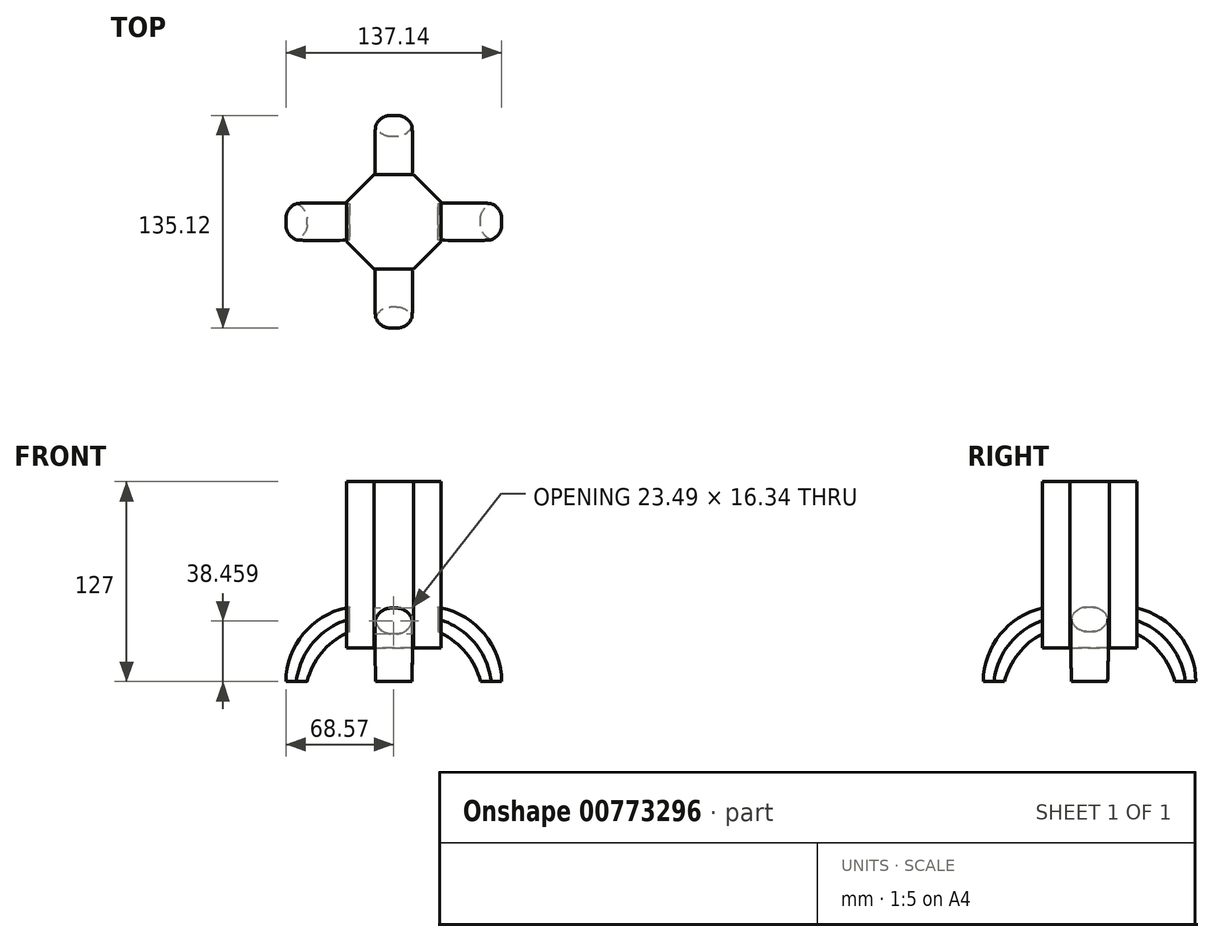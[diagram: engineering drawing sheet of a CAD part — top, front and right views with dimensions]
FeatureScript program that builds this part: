
annotation { "Feature Type Name" : "Feature", "Feature Type Description" : "" }
export const myFeature = defineFeature(function(context is Context, id is Id, definition is map)
    precondition{}
    {
        {
            var Q0;
            Q0=qCreatedBy(makeId("Top.planeOp"),FACE);
            var sketch = newSketch(context, id + "F0", { "sketchPlane" : qUnion([Q0])});
            skCircle(sketch, "E0.cCircle", {"center": v(0, 0) * mm, "radius": 30.08 * mm, "construction": true});
            skLineSegment(sketch, "E0.0", {"start": v(30.08, 12.46) * mm, "end": v(30.08, -12.46) * mm});
            skLineSegment(sketch, "E0.1", {"start": v(30.08, -12.46) * mm, "end": v(12.46, -30.08) * mm});
            skLineSegment(sketch, "E0.2", {"start": v(12.46, -30.08) * mm, "end": v(-12.46, -30.08) * mm});
            skLineSegment(sketch, "E0.3", {"start": v(-12.46, -30.08) * mm, "end": v(-30.08, -12.46) * mm});
            skLineSegment(sketch, "E0.4", {"start": v(-30.08, -12.46) * mm, "end": v(-30.08, 12.46) * mm});
            skLineSegment(sketch, "E0.5", {"start": v(-30.08, 12.46) * mm, "end": v(-12.46, 30.08) * mm});
            skLineSegment(sketch, "E0.6", {"start": v(-12.46, 30.08) * mm, "end": v(12.46, 30.08) * mm});
            skLineSegment(sketch, "E0.7", {"start": v(12.46, 30.08) * mm, "end": v(30.08, 12.46) * mm});
            skPoint(sketch, "E0.0.midPoint", {"position": v(30.08, 0) * mm});
            skSolve(sketch);
        }
        {
            var Q0;
            Q0 = qSketchRegion(id + "F0", true);
            extrude(context, id + "F1", {"entities" : qUnion([Q0]), "depth" : 127 * mm, "offsetDistance" : 25.4 * mm, "hasSecondDirection" : true, "secondDirectionOppositeDirection" : false, "secondDirectionDepth" : 21.34 * mm});
        }
        {
            var Q0;
            Q0=qCreatedBy(makeId("Front.planeOp"),FACE);
            var sketch = newSketch(context, id + "F2", { "sketchPlane" : qUnion([Q0])});
            skLineSegment(sketch, "E1", {"start": v(0, 0) * mm, "end": v(0, 165.92) * mm, "construction": true});
            skLineSegment(sketch, "E2", {"start": v(0, 165.92) * mm, "end": v(30.07, 127) * mm});
            skLineSegment(sketch, "E3", {"start": v(30.07, 127) * mm, "end": v(0, 127) * mm});
            skSolve(sketch);
        }
        {
            var Q0;
            Q0 = qSketchRegion(id + "F2", true);
            var Q1;
            Q1=sQuery(id+"F2.wireOp",EDGE,"E2");
            var Q2;
            Q2=sQuery(id+"F2.wireOp",EDGE,"E3");
            var Q3;
            Q3=sQuery(id+"F2.wireOp",EDGE,"E1");
            revolve(context, id + "F3", {"bodyType" : ToolBodyType.SURFACE, "surfaceOperationType" : NewSurfaceOperationType.NEW, "entities" : qUnion([Q0]), "surfaceEntities" : qUnion([Q1, Q2]), "axis" : qUnion([Q3]), "revolveType" : RevolveType.FULL});
        }
        {
            var Q0;
            Q0=qCreatedBy(makeId("Front.planeOp"),FACE);
            var sketch = newSketch(context, id + "F4", { "sketchPlane" : qUnion([Q0])});
            skArc(sketch, "E4", {"start": v(-28.1, 47.23) * mm, "mid": v(-56.89, 30.94) * mm, "end": v(-68.57, 0) * mm});
            skArc(sketch, "E5", {"start": v(-28.01, 31.76) * mm, "mid": v(-45.21, 19) * mm, "end": v(-55.09, 0) * mm});
            skLineSegment(sketch, "E6", {"start": v(-68.57, 0) * mm, "end": v(-55.09, 0) * mm});
            skLineSegment(sketch, "E7", {"start": v(-28.1, 47.23) * mm, "end": v(-28.01, 31.76) * mm});
            skLineSegment(sketch, "E8.MirrorCS", {"start": v(68.57, 0) * mm, "end": v(55.09, 0) * mm});
            skArc(sketch, "E9.MirrorCS", {"start": v(28.1, 47.23) * mm, "mid": v(56.89, 30.94) * mm, "end": v(68.57, 0) * mm});
            skLineSegment(sketch, "E10.MirrorCS", {"start": v(28.1, 47.23) * mm, "end": v(28.01, 31.76) * mm});
            skArc(sketch, "E11.MirrorCS", {"start": v(28.01, 31.76) * mm, "mid": v(45.21, 19) * mm, "end": v(55.09, 0) * mm});
            skSolve(sketch);
        }
        {
            var Q0;
            Q0=makeQuery(id+"F4.imprint","IMPRINT",FACE,{"disambiguationData":[TD([[makeQuery(id+"F4.imprint","IMPRINT",EDGE,{"derivedFrom":sQuery(id+"F4.wireOp",EDGE,"E4")}),1.0]])]});
            var Q1;
            Q1=makeQuery(id+"F4.imprint","IMPRINT",FACE,{"disambiguationData":[TD([[makeQuery(id+"F4.imprint","IMPRINT",EDGE,{"derivedFrom":sQuery(id+"F4.wireOp",EDGE,"E8.MirrorCS")}),-1.0]])]});
            extrude(context, id + "F5", {"entities" : qUnion([Q0, Q1]), "endBound" : BoundingType.SYMMETRIC, "depth" : 24.13 * mm, "offsetDistance" : 25.4 * mm});
        }
        {
            var Q0;
            Q0=makeQuery(id+"F5.opExtrude","CAP_EDGE",EDGE,{"disambiguationData":[OSD([sQuery(id+"F4.wireOp",EDGE,"E4")])],"isStart":false});
            var Q1;
            Q1=makeQuery(id+"F5.opExtrude","CAP_EDGE",EDGE,{"disambiguationData":[OSD([sQuery(id+"F4.wireOp",EDGE,"E5")])],"isStart":false});
            var Q2;
            Q2=makeQuery(id+"F5.opExtrude","CAP_EDGE",EDGE,{"disambiguationData":[OSD([sQuery(id+"F4.wireOp",EDGE,"E4")])],"isStart":true});
            var Q3;
            Q3=makeQuery(id+"F5.opExtrude","CAP_EDGE",EDGE,{"disambiguationData":[OSD([sQuery(id+"F4.wireOp",EDGE,"E5")])],"isStart":true});
            var Q4;
            Q4=makeQuery(id+"F5.opExtrude","CAP_EDGE",EDGE,{"disambiguationData":[OSD([sQuery(id+"F4.wireOp",EDGE,"E9.MirrorCS")])],"isStart":false});
            var Q5;
            Q5=makeQuery(id+"F5.opExtrude","CAP_EDGE",EDGE,{"disambiguationData":[OSD([sQuery(id+"F4.wireOp",EDGE,"E9.MirrorCS")])],"isStart":true});
            var Q6;
            Q6=makeQuery(id+"F5.opExtrude","CAP_EDGE",EDGE,{"disambiguationData":[OSD([sQuery(id+"F4.wireOp",EDGE,"E11.MirrorCS")])],"isStart":false});
            var Q7;
            Q7=makeQuery(id+"F5.opExtrude","CAP_EDGE",EDGE,{"disambiguationData":[OSD([sQuery(id+"F4.wireOp",EDGE,"E11.MirrorCS")])],"isStart":true});
            fillet(context, id + "F6", {"entities" : qUnion([Q0, Q1, Q2, Q3, Q4, Q5, Q6, Q7]), "radius" : 10.16 * mm, "tangentPropagation" : true, "allowEdgeOverflow" : false});
        }
        {
            var Q0;
            Q0=qCreatedBy(makeId("Right.planeOp"),FACE);
            var sketch = newSketch(context, id + "F7", { "sketchPlane" : qUnion([Q0])});
            skArc(sketch, "E12", {"start": v(-28.93, 46.88) * mm, "mid": v(-56.48, 30.23) * mm, "end": v(-67.56, 0) * mm});
            skArc(sketch, "E13", {"start": v(-28.83, 30.92) * mm, "mid": v(-44.85, 18.23) * mm, "end": v(-54.08, 0) * mm});
            skLineSegment(sketch, "E14", {"start": v(-67.56, 0) * mm, "end": v(-54.08, 0) * mm});
            skLineSegment(sketch, "E15", {"start": v(-28.93, 46.88) * mm, "end": v(-28.83, 30.92) * mm});
            skArc(sketch, "E16.MirrorCS", {"start": v(28.93, 46.88) * mm, "mid": v(56.48, 30.23) * mm, "end": v(67.56, 0) * mm});
            skLineSegment(sketch, "E17.MirrorCS", {"start": v(28.93, 46.88) * mm, "end": v(28.83, 30.92) * mm});
            skArc(sketch, "E18.MirrorCS", {"start": v(28.83, 30.92) * mm, "mid": v(44.85, 18.23) * mm, "end": v(54.08, 0) * mm});
            skLineSegment(sketch, "E19.MirrorCS", {"start": v(67.56, 0) * mm, "end": v(54.08, 0) * mm});
            skSolve(sketch);
        }
        {
            var Q0;
            Q0 = qSketchRegion(id + "F7", true);
            extrude(context, id + "F8", {"entities" : qUnion([Q0]), "operationType" : NewBodyOperationType.ADD, "endBound" : BoundingType.SYMMETRIC, "depth" : 24.13 * mm, "offsetDistance" : 25.4 * mm});
        }
        {
            var Q0;
            Q0=makeQuery(id+"F8.opExtrude","CAP_EDGE",EDGE,{"disambiguationData":[OSD([sQuery(id+"F7.wireOp",EDGE,"E12")])],"isStart":true});
            var Q1;
            Q1=makeQuery(id+"F8.opExtrude","CAP_EDGE",EDGE,{"disambiguationData":[OSD([sQuery(id+"F7.wireOp",EDGE,"E13")])],"isStart":true});
            var Q2;
            Q2=makeQuery(id+"F8.opExtrude","CAP_EDGE",EDGE,{"disambiguationData":[OSD([sQuery(id+"F7.wireOp",EDGE,"E12")])],"isStart":false});
            var Q3;
            Q3=makeQuery(id+"F8.opExtrude","CAP_EDGE",EDGE,{"disambiguationData":[OSD([sQuery(id+"F7.wireOp",EDGE,"E13")])],"isStart":false});
            var Q4;
            Q4=makeQuery(id+"F8.opExtrude","CAP_EDGE",EDGE,{"disambiguationData":[OSD([sQuery(id+"F7.wireOp",EDGE,"E16.MirrorCS")])],"isStart":false});
            var Q5;
            Q5=makeQuery(id+"F8.opExtrude","CAP_EDGE",EDGE,{"disambiguationData":[OSD([sQuery(id+"F7.wireOp",EDGE,"E16.MirrorCS")])],"isStart":true});
            var Q6;
            Q6=makeQuery(id+"F8.opExtrude","CAP_EDGE",EDGE,{"disambiguationData":[OSD([sQuery(id+"F7.wireOp",EDGE,"E18.MirrorCS")])],"isStart":false});
            var Q7;
            Q7=makeQuery(id+"F8.opExtrude","CAP_EDGE",EDGE,{"disambiguationData":[OSD([sQuery(id+"F7.wireOp",EDGE,"E18.MirrorCS")])],"isStart":true});
            fillet(context, id + "F9", {"entities" : qUnion([Q0, Q1, Q2, Q3, Q4, Q5, Q6, Q7]), "radius" : 10.16 * mm, "tangentPropagation" : true, "allowEdgeOverflow" : false});
        }
    });
